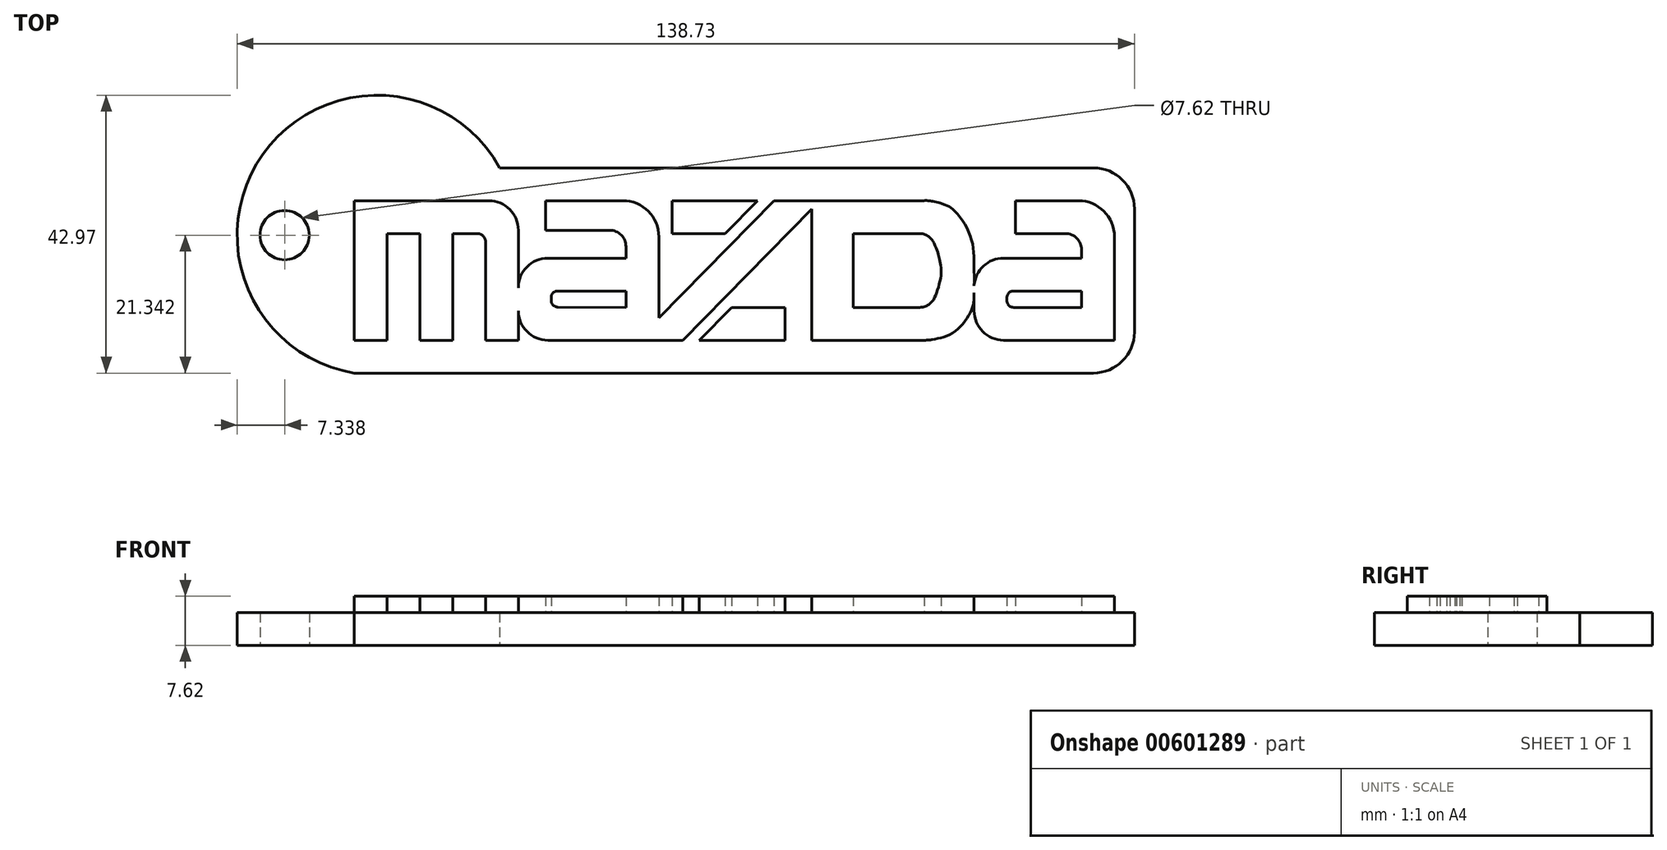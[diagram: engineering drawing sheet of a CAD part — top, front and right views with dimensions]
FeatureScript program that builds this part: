
annotation { "Feature Type Name" : "Feature", "Feature Type Description" : "" }
export const myFeature = defineFeature(function(context is Context, id is Id, definition is map)
    precondition{}
    {
        {
            var Q0;
            Q0=qCreatedBy(makeId("Top.planeOp"),FACE);
            var sketch = newSketch(context, id + "F0", { "sketchPlane" : qUnion([Q0])});
            skLineSegment(sketch, "E0.bottom", {"start": v(53.97, -15.87) * mm, "end": v(-60.33, -15.87) * mm});
            skLineSegment(sketch, "E0.top", {"start": v(53.98, 15.87) * mm, "end": v(-60.33, 15.88) * mm});
            skLineSegment(sketch, "E0.left", {"start": v(60.33, -9.52) * mm, "end": v(60.33, 9.53) * mm});
            skLineSegment(sketch, "E0.right", {"start": v(-60.33, -15.87) * mm, "end": v(-60.33, 15.88) * mm});
            skPoint(sketch, "E0.middle", {"position": v(0, 0) * mm});
            skPoint(sketch, "E1.visualSharp", {"position": v(60.33, 15.88) * mm});
            skArc(sketch, "E1.filletArc", {"start": v(60.33, 9.53) * mm, "mid": v(58.47, 14.02) * mm, "end": v(53.98, 15.88) * mm});
            skPoint(sketch, "E2.visualSharp", {"position": v(60.33, -15.87) * mm});
            skArc(sketch, "E2.filletArc", {"start": v(53.97, -15.87) * mm, "mid": v(58.47, -14.02) * mm, "end": v(60.33, -9.52) * mm});
            skCircle(sketch, "E3", {"center": v(-71.06, 5.46) * mm, "radius": 3.81 * mm});
            skArc(sketch, "E4", {"start": v(-37.81, 15.88) * mm, "mid": v(-74.42, 17.97) * mm, "end": v(-60.33, -15.87) * mm});
            skSolve(sketch);
        }
        {
            var Q0;
            Q0 = qSketchRegion(id + "F0", true);
            extrude(context, id + "F1", {"entities" : qUnion([Q0]), "depth" : 5.08 * mm, "offsetDistance" : 25.4 * mm});
        }
        {
            var Q0;
            Q0=makeQuery(id+"F1.opExtrude","CAP_FACE",FACE,{"disambiguationData":[OSD([sQuery(id+"F0.wireOp",EDGE,"E0.bottom"),sQuery(id+"F0.wireOp",EDGE,"E0.top"),sQuery(id+"F0.wireOp",EDGE,"E0.left"),sQuery(id+"F0.wireOp",EDGE,"E1.filletArc"),sQuery(id+"F0.wireOp",EDGE,"E2.filletArc"),sQuery(id+"F0.wireOp",EDGE,"E3"),sQuery(id+"F0.wireOp",EDGE,"E4")])],"isStart":false});
            var sketch = newSketch(context, id + "F2", { "sketchPlane" : qUnion([Q0])});
            skLineSegment(sketch, "E5", {"start": v(-60.33, 10.8) * mm, "end": v(-39.5, 10.8) * mm});
            skLineSegment(sketch, "E6", {"start": v(-34.92, 6.22) * mm, "end": v(-34.92, -10.8) * mm});
            skLineSegment(sketch, "E7", {"start": v(-34.92, -10.8) * mm, "end": v(-40, -10.8) * mm});
            skLineSegment(sketch, "E8", {"start": v(-40, -10.8) * mm, "end": v(-40, 4.44) * mm});
            skLineSegment(sketch, "E9", {"start": v(-41.27, 5.72) * mm, "end": v(-45.09, 5.72) * mm});
            skLineSegment(sketch, "E10", {"start": v(-45.09, 5.72) * mm, "end": v(-45.09, -10.8) * mm});
            skLineSegment(sketch, "E11", {"start": v(-45.09, -10.8) * mm, "end": v(-50.16, -10.8) * mm});
            skLineSegment(sketch, "E12", {"start": v(-50.16, -10.8) * mm, "end": v(-50.16, 5.72) * mm});
            skLineSegment(sketch, "E13", {"start": v(-50.16, 5.71) * mm, "end": v(-55.25, 5.71) * mm});
            skLineSegment(sketch, "E14", {"start": v(-55.25, 5.71) * mm, "end": v(-55.25, -10.8) * mm});
            skLineSegment(sketch, "E15", {"start": v(-55.25, -10.8) * mm, "end": v(-60.33, -10.8) * mm});
            skPoint(sketch, "E16.visualSharp", {"position": v(-34.92, 10.8) * mm});
            skArc(sketch, "E16.filletArc", {"start": v(-34.92, 6.22) * mm, "mid": v(-36.26, 9.46) * mm, "end": v(-39.5, 10.8) * mm});
            skPoint(sketch, "E17.visualSharp", {"position": v(-40, 5.72) * mm});
            skArc(sketch, "E17.filletArc", {"start": v(-40, 4.44) * mm, "mid": v(-40.38, 5.34) * mm, "end": v(-41.27, 5.71) * mm});
            skLineSegment(sketch, "E18", {"start": v(-34.92, -6.22) * mm, "end": v(-34.92, -2.67) * mm});
            skLineSegment(sketch, "E19", {"start": v(-30.35, 1.9) * mm, "end": v(-18.29, 1.9) * mm});
            skLineSegment(sketch, "E20", {"start": v(-18.29, 1.9) * mm, "end": v(-18.29, 3.68) * mm});
            skLineSegment(sketch, "E21", {"start": v(-30.7, 10.8) * mm, "end": v(-18.8, 10.8) * mm});
            skLineSegment(sketch, "E22", {"start": v(-13.2, -10.8) * mm, "end": v(-30.35, -10.8) * mm});
            skLineSegment(sketch, "E23", {"start": v(-29.84, -4.64) * mm, "end": v(-29.84, -4.2) * mm});
            skLineSegment(sketch, "E24", {"start": v(-28.83, -3.17) * mm, "end": v(-18.29, -3.17) * mm});
            skLineSegment(sketch, "E25", {"start": v(-18.29, -3.17) * mm, "end": v(-18.29, -5.71) * mm});
            skLineSegment(sketch, "E26", {"start": v(-18.29, -5.71) * mm, "end": v(-28.83, -5.66) * mm});
            skLineSegment(sketch, "E27", {"start": v(-20.83, 6.22) * mm, "end": v(-30.7, 6.22) * mm});
            skLineSegment(sketch, "E28", {"start": v(-30.7, 6.22) * mm, "end": v(-30.7, 10.8) * mm});
            skPoint(sketch, "E29.visualSharp", {"position": v(-34.92, -10.8) * mm});
            skArc(sketch, "E29.filletArc", {"start": v(-34.92, -6.22) * mm, "mid": v(-33.59, -9.46) * mm, "end": v(-30.35, -10.8) * mm});
            skPoint(sketch, "E30.visualSharp", {"position": v(-34.92, 1.9) * mm});
            skArc(sketch, "E30.filletArc", {"start": v(-30.35, 1.9) * mm, "mid": v(-33.59, 0.57) * mm, "end": v(-34.92, -2.67) * mm});
            skPoint(sketch, "E31.visualSharp", {"position": v(-29.84, -3.17) * mm});
            skArc(sketch, "E31.filletArc", {"start": v(-28.83, -3.17) * mm, "mid": v(-29.55, -3.47) * mm, "end": v(-29.84, -4.2) * mm});
            skPoint(sketch, "E32.visualSharp", {"position": v(-29.84, -5.65) * mm});
            skArc(sketch, "E32.filletArc", {"start": v(-29.84, -4.64) * mm, "mid": v(-29.55, -5.36) * mm, "end": v(-28.83, -5.66) * mm});
            skPoint(sketch, "E33.visualSharp", {"position": v(-18.29, 6.22) * mm});
            skArc(sketch, "E33.filletArc", {"start": v(-18.29, 3.68) * mm, "mid": v(-19.03, 5.48) * mm, "end": v(-20.83, 6.22) * mm});
            skLineSegment(sketch, "E34", {"start": v(-13.2, 5.2) * mm, "end": v(-13.2, -10.8) * mm});
            skPoint(sketch, "E35.visualSharp", {"position": v(-13.2, 10.8) * mm});
            skArc(sketch, "E35.filletArc", {"start": v(-13.2, 5.2) * mm, "mid": v(-14.84, 9.16) * mm, "end": v(-18.8, 10.8) * mm});
            skLineSegment(sketch, "E36", {"start": v(-13.2, -10.8) * mm, "end": v(-9.47, -10.8) * mm});
            skLineSegment(sketch, "E37", {"start": v(-9.47, -10.8) * mm, "end": v(11.68, 10.8) * mm});
            skLineSegment(sketch, "E38", {"start": v(11.68, 10.8) * mm, "end": v(4.57, 10.8) * mm});
            skLineSegment(sketch, "E39", {"start": v(4.57, 10.8) * mm, "end": v(-13.2, -7.35) * mm});
            skLineSegment(sketch, "E40", {"start": v(2.03, 10.8) * mm, "end": v(-2.95, 5.71) * mm});
            skLineSegment(sketch, "E41", {"start": v(-2.95, 5.72) * mm, "end": v(-11.18, 5.72) * mm});
            skLineSegment(sketch, "E42", {"start": v(-11.18, 5.72) * mm, "end": v(-11.18, 10.8) * mm});
            skLineSegment(sketch, "E43", {"start": v(-11.18, 10.8) * mm, "end": v(2.03, 10.8) * mm});
            skLineSegment(sketch, "E44", {"start": v(-6.93, -10.8) * mm, "end": v(6.28, -10.8) * mm});
            skLineSegment(sketch, "E45", {"start": v(6.28, -10.8) * mm, "end": v(6.28, -5.71) * mm});
            skLineSegment(sketch, "E46", {"start": v(6.28, -5.72) * mm, "end": v(-1.95, -5.72) * mm});
            skLineSegment(sketch, "E47", {"start": v(-1.95, -5.71) * mm, "end": v(-6.93, -10.8) * mm});
            skLineSegment(sketch, "E48", {"start": v(11.68, -10.8) * mm, "end": v(28.08, -10.8) * mm});
            skLineSegment(sketch, "E49", {"start": v(16.86, -5.71) * mm, "end": v(16.86, 5.72) * mm});
            skLineSegment(sketch, "E50", {"start": v(16.86, 5.72) * mm, "end": v(27.02, 5.72) * mm});
            skLineSegment(sketch, "E51", {"start": v(27.12, -5.71) * mm, "end": v(16.86, -5.71) * mm});
            skFitSpline(sketch, "E52", {"points": [v(28.65, 5.72) * mm, v(29.85, 3.02) * mm, v(30.2, 1.7) * mm, v(30.45, -0.4) * mm, v(29.67, -3.64) * mm, v(28.65, -5.71) * mm], "startDerivative": vector(5.15, -11.6) * mm, "endDerivative": vector(-6.2, -10.06) * mm});
            skArc(sketch, "E53.filletArc", {"start": v(29.33, 4.24) * mm, "mid": v(28.4, 5.31) * mm, "end": v(27.02, 5.72) * mm});
            skArc(sketch, "E54.filletArc", {"start": v(27.12, -5.71) * mm, "mid": v(28.51, -5.3) * mm, "end": v(29.45, -4.18) * mm});
            skFitSpline(sketch, "E55", {"points": [v(28.65, 10.8) * mm, v(33.07, 8.63) * mm, v(35, 5.23) * mm, v(35.53, 1.4) * mm, v(35.54, -3.45) * mm, v(35.13, -6.11) * mm, v(32.12, -9.74) * mm, v(28.65, -10.8) * mm], "startDerivative": vector(54.23, -10.79) * mm, "endDerivative": vector(-20.43, -5.31) * mm});
            skArc(sketch, "E56.filletArc", {"start": v(29.19, 10.68) * mm, "mid": v(28.52, 10.78) * mm, "end": v(27.84, 10.8) * mm});
            skArc(sketch, "E57.filletArc", {"start": v(28.08, -10.8) * mm, "mid": v(28.6, -10.77) * mm, "end": v(29.1, -10.69) * mm});
            skLineSegment(sketch, "E58", {"start": v(52.17, 1.9) * mm, "end": v(52.17, 3.18) * mm});
            skLineSegment(sketch, "E59", {"start": v(46.49, 10.8) * mm, "end": v(51.66, 10.8) * mm});
            skLineSegment(sketch, "E60", {"start": v(57.25, -10.8) * mm, "end": v(40.1, -10.8) * mm});
            skLineSegment(sketch, "E61", {"start": v(41.64, -3.17) * mm, "end": v(52.17, -3.17) * mm});
            skLineSegment(sketch, "E62", {"start": v(52.17, -3.17) * mm, "end": v(52.17, -5.71) * mm});
            skLineSegment(sketch, "E63", {"start": v(52.17, -5.71) * mm, "end": v(41.63, -5.71) * mm});
            skLineSegment(sketch, "E64", {"start": v(49.63, 5.72) * mm, "end": v(41.92, 5.72) * mm});
            skLineSegment(sketch, "E65", {"start": v(41.92, 5.72) * mm, "end": v(41.92, 6.22) * mm});
            skArc(sketch, "E66.filletArc", {"start": v(35.54, -6.22) * mm, "mid": v(36.88, -9.46) * mm, "end": v(40.1, -10.8) * mm});
            skArc(sketch, "E67.filletArc", {"start": v(41.64, -3.17) * mm, "mid": v(40.92, -3.47) * mm, "end": v(40.62, -4.2) * mm});
            skArc(sketch, "E68.filletArc", {"start": v(40.62, -4.7) * mm, "mid": v(40.92, -5.42) * mm, "end": v(41.63, -5.71) * mm});
            skArc(sketch, "E69.filletArc", {"start": v(52.17, 3.18) * mm, "mid": v(51.42, 4.97) * mm, "end": v(49.63, 5.72) * mm});
            skLineSegment(sketch, "E70", {"start": v(57.25, 5.2) * mm, "end": v(57.25, -10.8) * mm});
            skArc(sketch, "E71.filletArc", {"start": v(57.25, 5.2) * mm, "mid": v(55.61, 9.16) * mm, "end": v(51.66, 10.8) * mm});
            skLineSegment(sketch, "E72", {"start": v(35.54, -6.22) * mm, "end": v(35.54, -2.67) * mm});
            skPoint(sketch, "E73.visualSharp", {"position": v(41.92, 10.8) * mm});
            skLineSegment(sketch, "E74", {"start": v(41.92, 6.22) * mm, "end": v(41.92, 10.8) * mm});
            skLineSegment(sketch, "E75", {"start": v(46.49, 10.8) * mm, "end": v(41.92, 10.8) * mm});
            skLineSegment(sketch, "E76", {"start": v(40.1, 1.9) * mm, "end": v(52.17, 1.9) * mm});
            skPoint(sketch, "E77.visualSharp", {"position": v(35.54, 1.9) * mm});
            skArc(sketch, "E77.filletArc", {"start": v(40.1, 1.9) * mm, "mid": v(36.88, 0.57) * mm, "end": v(35.54, -2.67) * mm});
            skLineSegment(sketch, "E78", {"start": v(40.62, -4.7) * mm, "end": v(40.62, -4.2) * mm});
            skLineSegment(sketch, "E79", {"start": v(-55.23, 10.8) * mm, "end": v(-60.33, 10.8) * mm});
            skLineSegment(sketch, "E80", {"start": v(-60.33, -10.8) * mm, "end": v(-55.23, -10.8) * mm});
            skLineSegment(sketch, "E81", {"start": v(-60.33, -10.8) * mm, "end": v(-60.33, 10.8) * mm});
            skLineSegment(sketch, "E82", {"start": v(-60.33, 10.8) * mm, "end": v(-55.23, 10.8) * mm});
            skLineSegment(sketch, "E83", {"start": v(11.68, -10.8) * mm, "end": v(10.43, -10.8) * mm});
            skLineSegment(sketch, "E84", {"start": v(10.43, -10.8) * mm, "end": v(10.43, 9.51) * mm});
            skLineSegment(sketch, "E85", {"start": v(10.43, 9.51) * mm, "end": v(11.68, 10.8) * mm});
            skLineSegment(sketch, "E86", {"start": v(27.84, 10.8) * mm, "end": v(11.68, 10.8) * mm});
            skSolve(sketch);
        }
        {
            var Q0;
            Q0 = qSketchRegion(id + "F2", true);
            extrude(context, id + "F3", {"entities" : qUnion([Q0]), "operationType" : NewBodyOperationType.ADD, "depth" : 2.54 * mm, "offsetDistance" : 25.4 * mm});
        }
    });
